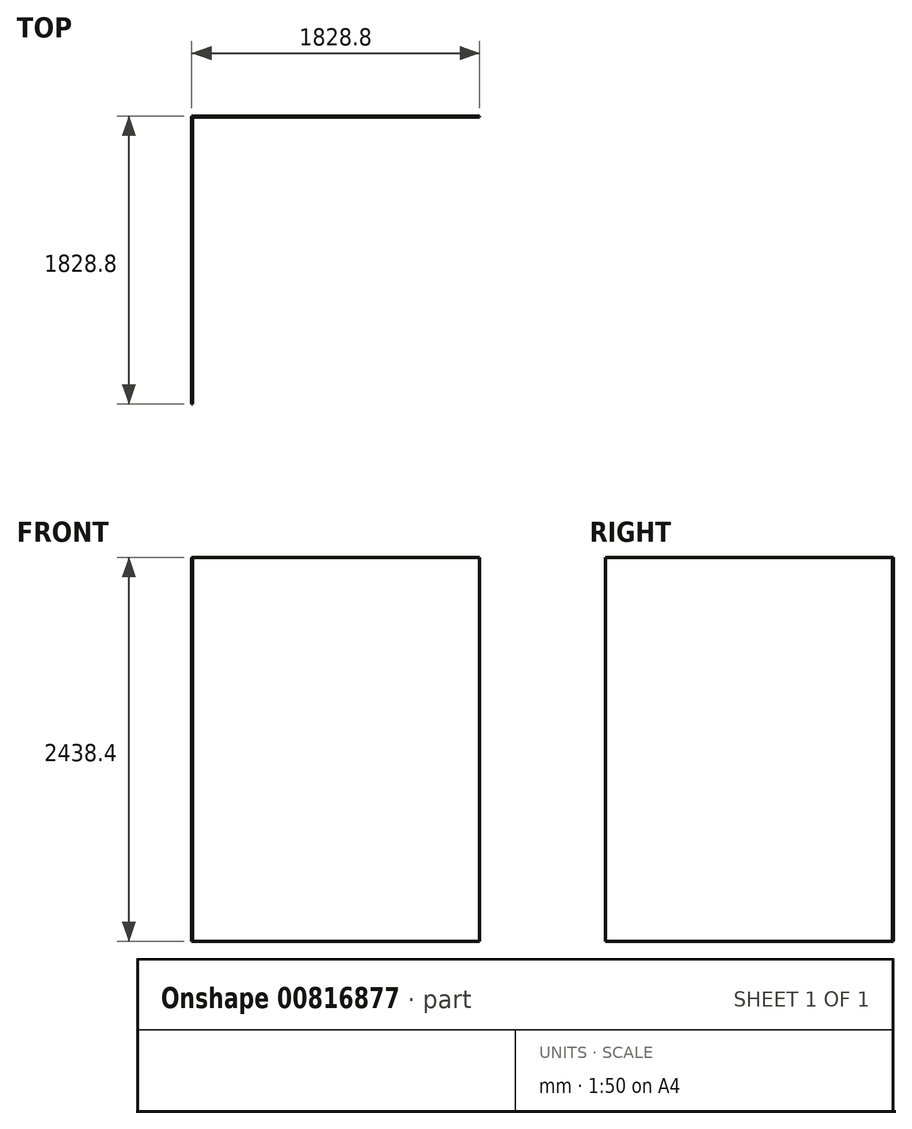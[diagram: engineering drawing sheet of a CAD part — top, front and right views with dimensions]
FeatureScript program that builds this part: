
annotation { "Feature Type Name" : "Feature", "Feature Type Description" : "" }
export const myFeature = defineFeature(function(context is Context, id is Id, definition is map)
    precondition{}
    {
        {
            var Q0;
            Q0=qCreatedBy(makeId("Top.planeOp"),FACE);
            var sketch = newSketch(context, id + "F0", { "sketchPlane" : qUnion([Q0])});
            skLineSegment(sketch, "E0", {"start": v(0, -1828.8) * mm, "end": v(0, 0) * mm});
            skLineSegment(sketch, "E1", {"start": v(0, 0) * mm, "end": v(1828.8, 0) * mm});
            skLineSegment(sketch, "E2.0", {"start": v(6.35, -6.35) * mm, "end": v(1828.8, -6.35) * mm});
            skLineSegment(sketch, "E2.1", {"start": v(6.35, -1828.8) * mm, "end": v(6.35, -6.35) * mm});
            skLineSegment(sketch, "E3", {"start": v(1828.8, 0) * mm, "end": v(1828.8, -6.35) * mm});
            skLineSegment(sketch, "E4", {"start": v(0, -1828.8) * mm, "end": v(6.35, -1828.8) * mm});
            skSolve(sketch);
        }
        {
            var Q0;
            Q0 = qSketchRegion(id + "F0", true);
            extrude(context, id + "F1", {"entities" : qUnion([Q0]), "depth" : 2438.4 * mm, "offsetDistance" : 25.4 * mm});
        }
    });
